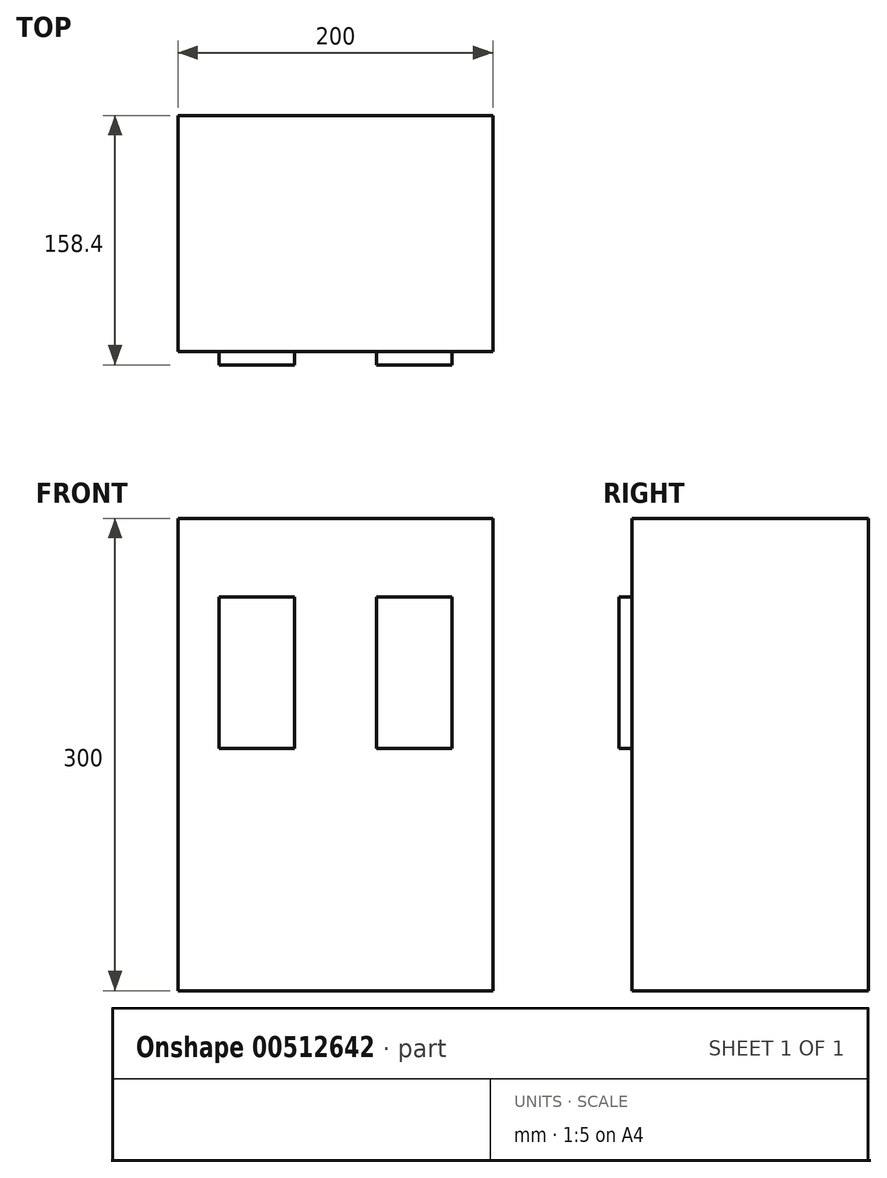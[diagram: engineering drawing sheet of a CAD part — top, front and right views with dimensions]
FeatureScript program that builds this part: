
annotation { "Feature Type Name" : "Feature", "Feature Type Description" : "" }
export const myFeature = defineFeature(function(context is Context, id is Id, definition is map)
    precondition{}
    {
        {
            var Q0;
            Q0=qCreatedBy(makeId("Front.planeOp"),FACE);
            var sketch = newSketch(context, id + "F0", { "sketchPlane" : qUnion([Q0])});
            skLineSegment(sketch, "E0.bottom", {"start": v(0, 300) * mm, "end": v(200, 300) * mm});
            skLineSegment(sketch, "E0.top", {"start": v(0, 0) * mm, "end": v(200, 0) * mm});
            skLineSegment(sketch, "E0.left", {"start": v(0, 300) * mm, "end": v(0, 0) * mm});
            skLineSegment(sketch, "E0.right", {"start": v(200, 300) * mm, "end": v(200, 0) * mm});
            skSolve(sketch);
        }
        {
            var Q0;
            Q0=makeQuery(id+"F0.imprint","IMPRINT",FACE,{"disambiguationData":[TD([[makeQuery(id+"F0.imprint","IMPRINT",EDGE,{"derivedFrom":sQuery(id+"F0.wireOp",EDGE,"E0.bottom")}),-1.0]])]});
            extrude(context, id + "F1", {"entities" : qUnion([Q0]), "depth" : 150 * mm});
        }
        {
            var Q0;
            Q0=makeQuery(id+"F1.opExtrude","CAP_FACE",FACE,{"disambiguationData":[OSD([sQuery(id+"F0.wireOp",EDGE,"E0.bottom"),sQuery(id+"F0.wireOp",EDGE,"E0.top"),sQuery(id+"F0.wireOp",EDGE,"E0.left"),sQuery(id+"F0.wireOp",EDGE,"E0.right")])],"isStart":false});
            var sketch = newSketch(context, id + "F2", { "sketchPlane" : qUnion([Q0])});
            skLineSegment(sketch, "E1.bottom", {"start": v(26, 250) * mm, "end": v(74, 250) * mm});
            skLineSegment(sketch, "E1.top", {"start": v(26, 154) * mm, "end": v(74, 154) * mm});
            skLineSegment(sketch, "E1.left", {"start": v(26, 250) * mm, "end": v(26, 154) * mm});
            skLineSegment(sketch, "E1.right", {"start": v(74, 250) * mm, "end": v(74, 154) * mm});
            skLineSegment(sketch, "E2.bottom", {"start": v(126, 250) * mm, "end": v(174, 250) * mm});
            skLineSegment(sketch, "E2.top", {"start": v(126, 154) * mm, "end": v(174, 154) * mm});
            skLineSegment(sketch, "E2.left", {"start": v(126, 250) * mm, "end": v(126, 154) * mm});
            skLineSegment(sketch, "E2.right", {"start": v(174, 250) * mm, "end": v(174, 154) * mm});
            skLineSegment(sketch, "E3", {"start": v(100, 300) * mm, "end": v(100, 0) * mm, "construction": true});
            skLineSegment(sketch, "E4", {"start": v(100, 300) * mm, "end": v(200, 300) * mm, "construction": true});
            skLineSegment(sketch, "E5", {"start": v(100, 300) * mm, "end": v(0, 300) * mm, "construction": true});
            skLineSegment(sketch, "E6", {"start": v(50, 300) * mm, "end": v(50, 250) * mm, "construction": true});
            skLineSegment(sketch, "E7", {"start": v(150, 300) * mm, "end": v(150, 250) * mm, "construction": true});
            skLineSegment(sketch, "E8", {"start": v(50, 250) * mm, "end": v(50, 0) * mm, "construction": true});
            skLineSegment(sketch, "E9", {"start": v(150, 250) * mm, "end": v(150, 0) * mm, "construction": true});
            skSolve(sketch);
        }
        {
            var Q0;
            Q0 = qSketchRegion(id + "F2", true);
            extrude(context, id + "F3", {"entities" : qUnion([Q0]), "depth" : 8.4 * mm});
        }
    });
